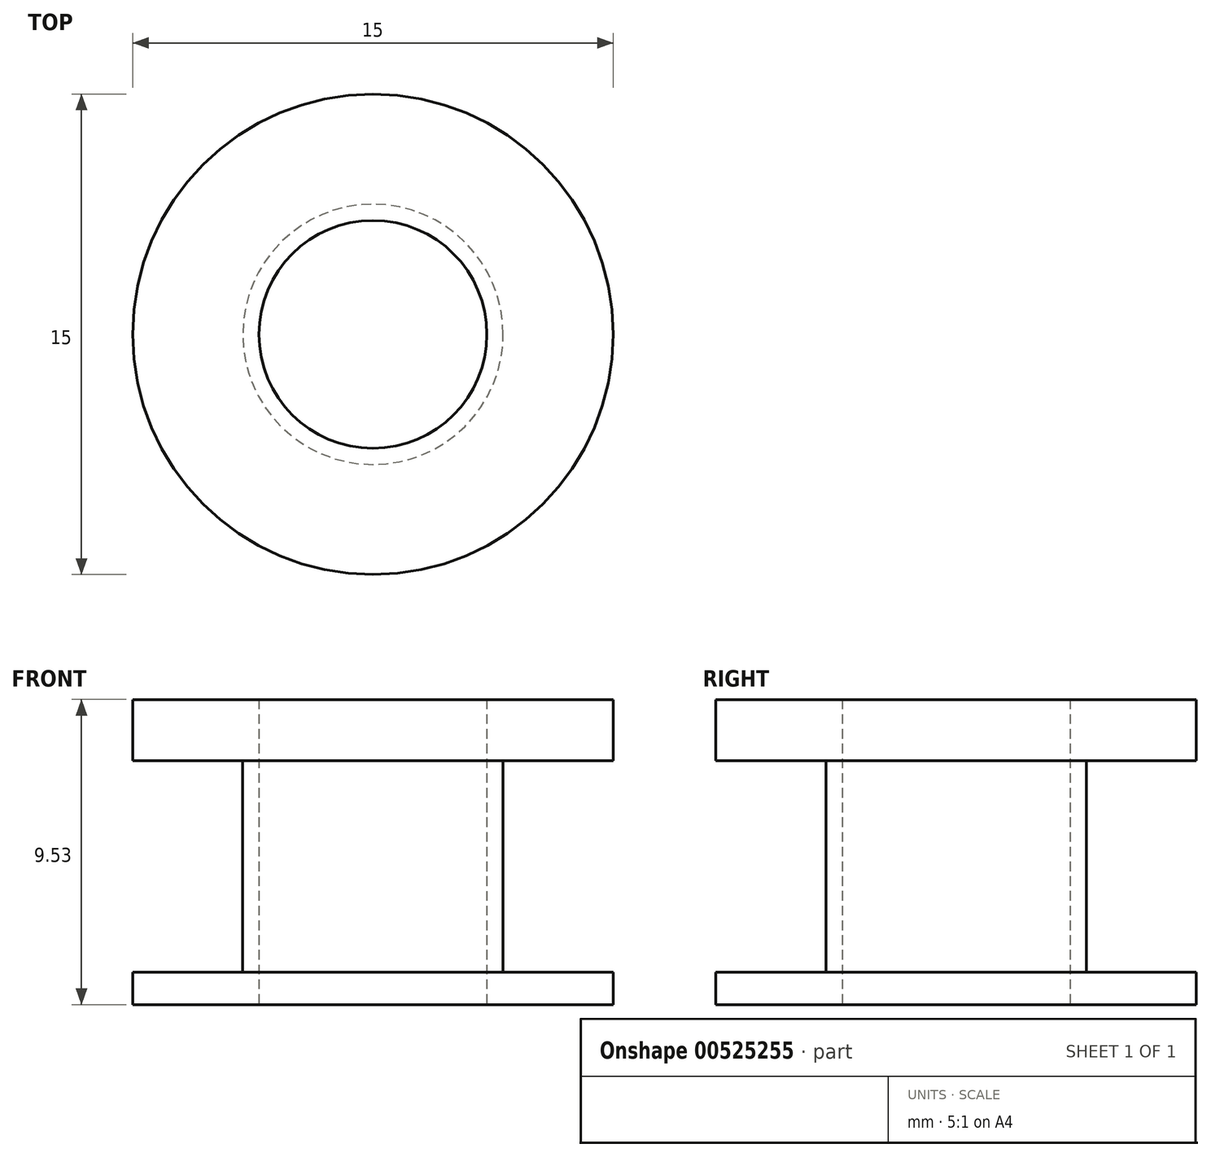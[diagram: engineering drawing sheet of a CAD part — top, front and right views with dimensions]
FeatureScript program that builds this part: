
annotation { "Feature Type Name" : "Feature", "Feature Type Description" : "" }
export const myFeature = defineFeature(function(context is Context, id is Id, definition is map)
    precondition{}
    {
        {
            var Q0;
            Q0=qCreatedBy(makeId("Top.planeOp"),FACE);
            var sketch = newSketch(context, id + "F0", { "sketchPlane" : qUnion([Q0])});
            skCircle(sketch, "E0", {"center": v(0, 0) * mm, "radius": 3.56 * mm});
            skCircle(sketch, "E1", {"center": v(0, 0) * mm, "radius": 7.5 * mm});
            skSolve(sketch);
        }
        {
            var Q0;
            Q0=makeQuery(id+"F0.imprint","IMPRINT",FACE,{"disambiguationData":[TD([[makeQuery(id+"F0.imprint","IMPRINT",EDGE,{"derivedFrom":sQuery(id+"F0.wireOp",EDGE,"E0")}),-1.0]])]});
            extrude(context, id + "F1", {"entities" : qUnion([Q0]), "depth" : 9.52 * mm, "offsetDistance" : 25.4 * mm});
        }
        {
            var Q0;
            Q0=qCreatedBy(makeId("Front.planeOp"),FACE);
            var sketch = newSketch(context, id + "F2", { "sketchPlane" : qUnion([Q0])});
            skLineSegment(sketch, "E2.left", {"start": v(4.06, 1.02) * mm, "end": v(4.06, 7.62) * mm});
            skLineSegment(sketch, "E3", {"start": v(4.06, 7.62) * mm, "end": v(19.06, 7.62) * mm});
            skLineSegment(sketch, "E4", {"start": v(4.06, 1.02) * mm, "end": v(19.06, 1.02) * mm});
            skLineSegment(sketch, "E5", {"start": v(19.06, 1.02) * mm, "end": v(19.06, 7.62) * mm});
            skSolve(sketch);
        }
        {
            var Q0;
            Q0=qCreatedBy(makeId("Front.planeOp"),FACE);
            var sketch = newSketch(context, id + "F3", { "sketchPlane" : qUnion([Q0])});
            skLineSegment(sketch, "E6", {"start": v(0, 0) * mm, "end": v(0, 10.18) * mm});
            skSolve(sketch);
        }
        {
            var Q0;
            Q0 = qSketchRegion(id + "F2", true);
            var Q1;
            Q1=sQuery(id+"F3.wireOp",EDGE,"E6");
            revolve(context, id + "F4", {"operationType" : NewBodyOperationType.REMOVE, "entities" : qUnion([Q0]), "axis" : qUnion([Q1]), "revolveType" : RevolveType.FULL, "oppositeDirection" : true});
        }
    });
